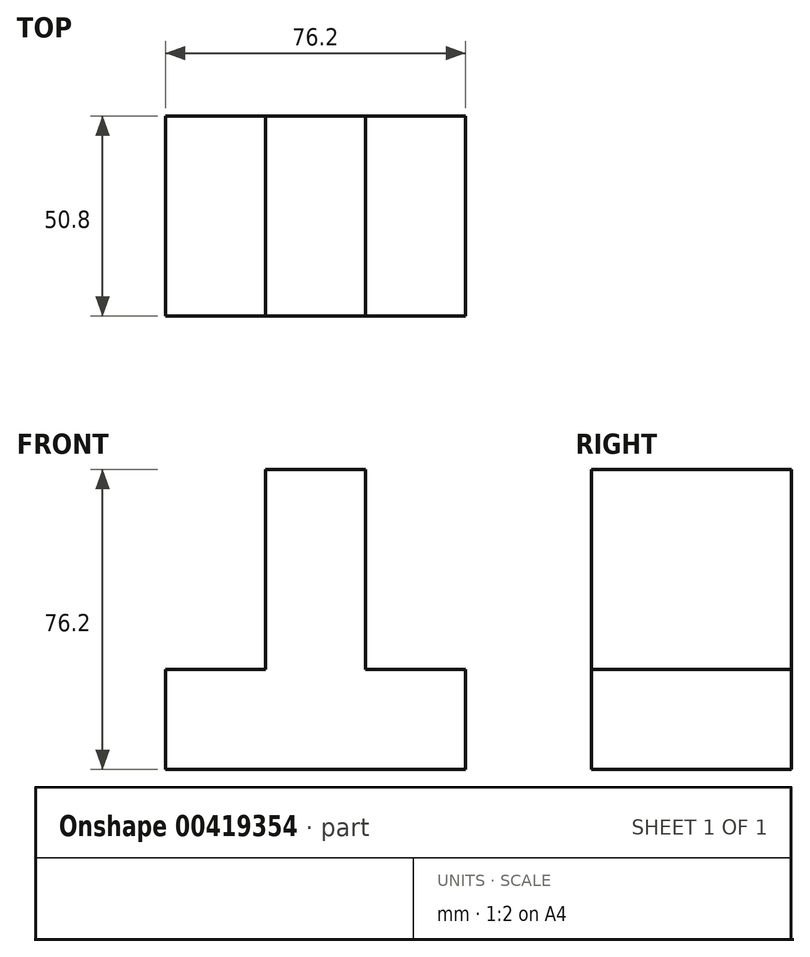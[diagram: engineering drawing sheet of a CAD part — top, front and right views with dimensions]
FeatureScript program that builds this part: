
annotation { "Feature Type Name" : "Feature", "Feature Type Description" : "" }
export const myFeature = defineFeature(function(context is Context, id is Id, definition is map)
    precondition{}
    {
        {
            var Q0;
            Q0=qCreatedBy(makeId("Front.planeOp"),FACE);
            var sketch = newSketch(context, id + "F0", { "sketchPlane" : qUnion([Q0])});
            skLineSegment(sketch, "E0", {"start": v(-15.66, 64.93) * mm, "end": v(-15.66, 14.13) * mm});
            skLineSegment(sketch, "E1", {"start": v(-15.66, 14.13) * mm, "end": v(-41.06, 14.13) * mm});
            skLineSegment(sketch, "E2", {"start": v(-41.06, 14.13) * mm, "end": v(-41.06, -11.27) * mm});
            skLineSegment(sketch, "E3", {"start": v(-41.06, -11.27) * mm, "end": v(35.14, -11.27) * mm});
            skLineSegment(sketch, "E4", {"start": v(35.14, -11.27) * mm, "end": v(35.14, 14.13) * mm});
            skLineSegment(sketch, "E5", {"start": v(35.14, 14.13) * mm, "end": v(9.74, 14.13) * mm});
            skLineSegment(sketch, "E6", {"start": v(9.74, 14.13) * mm, "end": v(9.74, 64.93) * mm});
            skLineSegment(sketch, "E7", {"start": v(9.74, 64.93) * mm, "end": v(-15.66, 64.93) * mm});
            skSolve(sketch);
        }
        {
            var Q0;
            Q0 = qSketchRegion(id + "F0", true);
            extrude(context, id + "F1", {"entities" : qUnion([Q0]), "depth" : 50.8 * mm});
        }
    });
